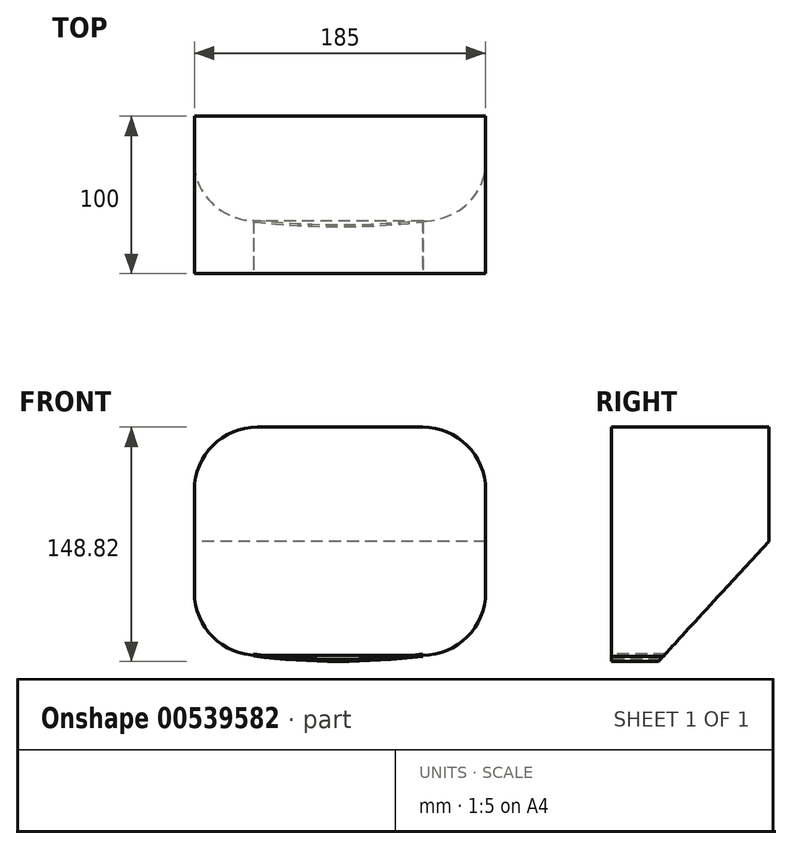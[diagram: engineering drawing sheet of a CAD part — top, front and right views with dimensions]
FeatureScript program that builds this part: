
annotation { "Feature Type Name" : "Feature", "Feature Type Description" : "" }
export const myFeature = defineFeature(function(context is Context, id is Id, definition is map)
    precondition{}
    {
        {
            var Q0;
            Q0=qCreatedBy(makeId("Front.planeOp"),FACE);
            var sketch = newSketch(context, id + "F0", { "sketchPlane" : qUnion([Q0])});
            skLineSegment(sketch, "E0.bottom", {"start": v(52.5, 72.5) * mm, "end": v(-52.5, 72.5) * mm});
            skLineSegment(sketch, "E0.top", {"start": v(52.5, -72.5) * mm, "end": v(-52.5, -72.5) * mm});
            skLineSegment(sketch, "E0.left", {"start": v(92.5, 32.5) * mm, "end": v(92.5, -32.5) * mm});
            skLineSegment(sketch, "E0.right", {"start": v(-92.5, 32.5) * mm, "end": v(-92.5, -32.5) * mm});
            skPoint(sketch, "E0.middle", {"position": v(0, 0) * mm});
            skPoint(sketch, "E1.visualSharp", {"position": v(-92.5, 72.5) * mm});
            skArc(sketch, "E1.filletArc", {"start": v(-52.5, 72.5) * mm, "mid": v(-80.78, 60.78) * mm, "end": v(-92.5, 32.5) * mm});
            skPoint(sketch, "E2.visualSharp", {"position": v(92.5, 72.5) * mm});
            skArc(sketch, "E2.filletArc", {"start": v(92.5, 32.5) * mm, "mid": v(80.78, 60.78) * mm, "end": v(52.5, 72.5) * mm});
            skPoint(sketch, "E3.visualSharp", {"position": v(92.5, -72.5) * mm});
            skArc(sketch, "E3.filletArc", {"start": v(52.5, -72.5) * mm, "mid": v(80.78, -60.78) * mm, "end": v(92.5, -32.5) * mm});
            skPoint(sketch, "E4.visualSharp", {"position": v(-92.5, -72.5) * mm});
            skArc(sketch, "E4.filletArc", {"start": v(-92.5, -32.5) * mm, "mid": v(-80.78, -60.78) * mm, "end": v(-52.5, -72.5) * mm});
            skSolve(sketch);
        }
        {
            var Q0;
            Q0 = qSketchRegion(id + "F0", true);
            extrude(context, id + "F1", {"entities" : qUnion([Q0]), "depth" : 100 * mm, "offsetDistance" : 25 * mm});
        }
        {
            var Q0;
            Q0=makeQuery(id+"F1.opExtrude","CAP_FACE",FACE,{"disambiguationData":[OSD([sQuery(id+"F0.wireOp",EDGE,"E0.bottom"),sQuery(id+"F0.wireOp",EDGE,"E0.top"),sQuery(id+"F0.wireOp",EDGE,"E0.left"),sQuery(id+"F0.wireOp",EDGE,"E0.right"),sQuery(id+"F0.wireOp",EDGE,"E1.filletArc"),sQuery(id+"F0.wireOp",EDGE,"E2.filletArc"),sQuery(id+"F0.wireOp",EDGE,"E3.filletArc"),sQuery(id+"F0.wireOp",EDGE,"E4.filletArc")])],"isStart":false});
            var sketch = newSketch(context, id + "F2", { "sketchPlane" : qUnion([Q0])});
            skArc(sketch, "E5", {"start": v(-55, -72.42) * mm, "mid": v(-1.25, -75.79) * mm, "end": v(52.5, -72.5) * mm});
            skArc(sketch, "E6", {"start": v(-54.84, -73.75) * mm, "mid": v(-1.1, -77.12) * mm, "end": v(52.66, -73.83) * mm});
            skLineSegment(sketch, "E7", {"start": v(-55, -72.42) * mm, "end": v(-54.84, -73.75) * mm});
            skLineSegment(sketch, "E8", {"start": v(52.5, -72.5) * mm, "end": v(52.66, -73.83) * mm});
            skSolve(sketch);
        }
        {
            var Q0;
            Q0=makeQuery(id+"F2.imprint","IMPRINT",FACE,{"disambiguationData":[TD([[makeQuery(id+"F2.imprint","IMPRINT",EDGE,{"derivedFrom":sQuery(id+"F2.wireOp",EDGE,"E5")}),-1.0]])]});
            extrude(context, id + "F3", {"entities" : qUnion([Q0]), "oppositeDirection" : true, "depth" : 100 * mm, "offsetDistance" : 25 * mm});
        }
        {
            var Q0;
            Q0=makeQuery(id+"F3.opExtrude","SWEPT_BODY",BODY,{"disambiguationData":[OSD([sQuery(id+"F2.wireOp",EDGE,"E5"),sQuery(id+"F2.wireOp",EDGE,"E6"),sQuery(id+"F2.wireOp",EDGE,"E7"),sQuery(id+"F2.wireOp",EDGE,"E8")])]});
            transform(context, id + "F4", {"entities" : qUnion([Q0]), "transformType" : TransformType.TRANSLATION_3D, "dx" : 0 * mm, "dy" : 0 * mm, "dz" : 0.8 * mm, "makeCopy" : false});
        }
        {
            var Q0;
            Q0=makeQuery(id+"F1.opExtrude","SWEPT_FACE",FACE,{"disambiguationData":[OSD([sQuery(id+"F0.wireOp",EDGE,"E0.right")])]});
            var sketch = newSketch(context, id + "F5", { "sketchPlane" : qUnion([Q0])});
            skLineSegment(sketch, "E9", {"start": v(100, -76.83) * mm, "end": v(70.68, -76.83) * mm});
            skLineSegment(sketch, "E10", {"start": v(70.68, -76.83) * mm, "end": v(0, 0) * mm});
            skLineSegment(sketch, "E11", {"start": v(0, 0) * mm, "end": v(-12.7, 0) * mm});
            skLineSegment(sketch, "E12", {"start": v(-12.7, 0) * mm, "end": v(-12.7, -86.1) * mm});
            skLineSegment(sketch, "E13", {"start": v(-12.7, -86.1) * mm, "end": v(70.68, -86.1) * mm});
            skLineSegment(sketch, "E14", {"start": v(70.68, -86.1) * mm, "end": v(70.68, -76.83) * mm});
            skSolve(sketch);
        }
        {
            var Q0;
            Q0 = qSketchRegion(id + "F5", true);
            extrude(context, id + "F6", {"entities" : qUnion([Q0]), "operationType" : NewBodyOperationType.REMOVE, "endBound" : BoundingType.THROUGH_ALL, "oppositeDirection" : true, "depth" : 25 * mm, "offsetDistance" : 25 * mm});
        }
    });
